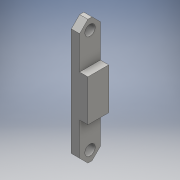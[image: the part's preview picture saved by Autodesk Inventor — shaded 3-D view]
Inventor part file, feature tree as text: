
AUTODESK INVENTOR PART (.ipt)
format: ipt  version: 2016 (Build 200138000, 138)  size: 135,680 bytes
history: native  units: mm
features: extrude x5, sketch x5, chamfer x4, other x2
ambient origin geometry x8: Origin, YZ Plane, XZ Plane, XY Plane, X Axis, Y Axis, Z Axis, Center Point
bodies: Body1 (feature_tree)
feature tree (16):
  other  "ソリッド1"
  extrude  "押し出し1"  Depth=4.0mm
  extrude  "押し出し2"  Depth=30.0mm
  extrude  "押し出し4"  Depth=5.0mm TaperAngle=0.0deg
  other  "作業平面1"
  extrude  "押し出し5"  Depth=2.0mm
  chamfer  "面取り1"  Distance=10.0mm
  chamfer  "面取り2"  Distance=5.0mm
  chamfer  "面取り3"  Distance=2.5mm
  chamfer  "面取り4"  Distance=5.0mm
  extrude  "押し出し6"  Depth=2.5mm
  sketch  "スケッチ1"
  sketch  "スケッチ2"
  sketch  "スケッチ4"
  sketch  "スケッチ5"
  sketch  "スケッチ6"
